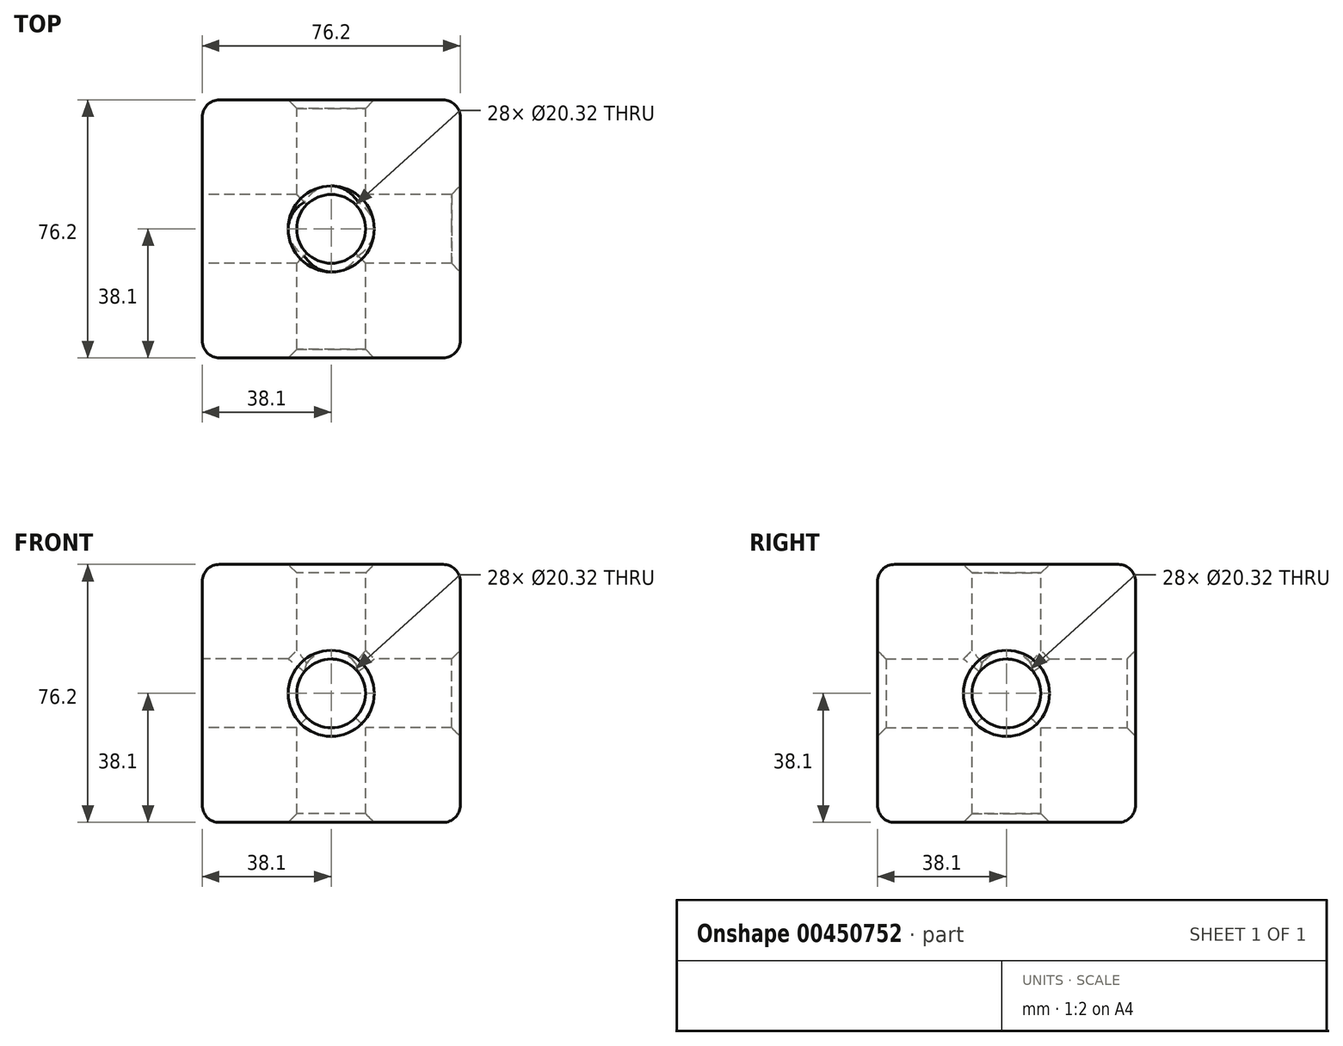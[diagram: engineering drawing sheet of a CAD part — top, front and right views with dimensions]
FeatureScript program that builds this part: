
annotation { "Feature Type Name" : "Feature", "Feature Type Description" : "" }
export const myFeature = defineFeature(function(context is Context, id is Id, definition is map)
    precondition{}
    {
        {
            var Q0;
            Q0=qCreatedBy(makeId("Top.planeOp"),FACE);
            var sketch = newSketch(context, id + "F0", { "sketchPlane" : qUnion([Q0])});
            skLineSegment(sketch, "E0.bottom", {"start": v(-38.1, 38.1) * mm, "end": v(38.1, 38.1) * mm});
            skLineSegment(sketch, "E0.top", {"start": v(-38.1, -38.1) * mm, "end": v(38.1, -38.1) * mm});
            skLineSegment(sketch, "E0.left", {"start": v(-38.1, 38.1) * mm, "end": v(-38.1, -38.1) * mm});
            skLineSegment(sketch, "E0.right", {"start": v(38.1, 38.1) * mm, "end": v(38.1, -38.1) * mm});
            skPoint(sketch, "E0.middle", {"position": v(0, 0) * mm});
            skSolve(sketch);
        }
        {
            var Q0;
            Q0 = qSketchRegion(id + "F0", true);
            extrude(context, id + "F1", {"entities" : qUnion([Q0]), "endBound" : BoundingType.SYMMETRIC, "depth" : 76.2 * mm});
        }
        {
            var Q0;
            Q0=qCreatedBy(makeId("Top.planeOp"),FACE);
            var sketch = newSketch(context, id + "F2", { "sketchPlane" : qUnion([Q0])});
            skCircle(sketch, "E1", {"center": v(0, 0) * mm, "radius": 10.16 * mm});
            skSolve(sketch);
        }
        {
            var Q0;
            Q0 = qSketchRegion(id + "F2", true);
            extrude(context, id + "F3", {"entities" : qUnion([Q0]), "operationType" : NewBodyOperationType.REMOVE, "endBound" : BoundingType.SYMMETRIC, "oppositeDirection" : true, "depth" : 319.53 * mm});
        }
        {
            var Q0;
            Q0=makeQuery(id+"F1.opExtrude","SWEPT_FACE",FACE,{"disambiguationData":[OSD([sQuery(id+"F0.wireOp",EDGE,"E0.left")])]});
            var sketch = newSketch(context, id + "F4", { "sketchPlane" : qUnion([Q0])});
            skCircle(sketch, "E2", {"center": v(0, 0) * mm, "radius": 10.16 * mm});
            skSolve(sketch);
        }
        {
            var Q0;
            Q0 = qSketchRegion(id + "F4", true);
            extrude(context, id + "F5", {"entities" : qUnion([Q0]), "operationType" : NewBodyOperationType.REMOVE, "oppositeDirection" : true, "depth" : 130.05 * mm});
        }
        {
            var Q0;
            Q0=makeQuery(id+"F1.opExtrude","SWEPT_FACE",FACE,{"disambiguationData":[OSD([sQuery(id+"F0.wireOp",EDGE,"E0.bottom")])]});
            var sketch = newSketch(context, id + "F6", { "sketchPlane" : qUnion([Q0])});
            skCircle(sketch, "E3", {"center": v(0, 0) * mm, "radius": 10.16 * mm});
            skSolve(sketch);
        }
        {
            var Q0;
            Q0 = qSketchRegion(id + "F6", true);
            extrude(context, id + "F7", {"entities" : qUnion([Q0]), "operationType" : NewBodyOperationType.REMOVE, "oppositeDirection" : true, "depth" : 100.08 * mm});
        }
        {
            var Q0;
            Q0=makeQuery(id+"F1.opExtrude","SWEPT_EDGE",EDGE,{"disambiguationData":[OSD([sQuery(id+"F0.wireOp",EDGE,"E0.bottom"),sQuery(id+"F0.wireOp",EDGE,"E0.left")])]});
            var Q1;
            Q1=makeQuery(id+"F1.opExtrude","CAP_EDGE",EDGE,{"disambiguationData":[OSD([sQuery(id+"F0.wireOp",EDGE,"E0.left")])],"isStart":true});
            var Q2;
            Q2=makeQuery(id+"F1.opExtrude","SWEPT_EDGE",EDGE,{"disambiguationData":[OSD([sQuery(id+"F0.wireOp",EDGE,"E0.top"),sQuery(id+"F0.wireOp",EDGE,"E0.left")])]});
            var Q3;
            Q3=makeQuery(id+"F1.opExtrude","CAP_EDGE",EDGE,{"disambiguationData":[OSD([sQuery(id+"F0.wireOp",EDGE,"E0.left")])],"isStart":false});
            var Q4;
            Q4=makeQuery(id+"F1.opExtrude","CAP_EDGE",EDGE,{"disambiguationData":[OSD([sQuery(id+"F0.wireOp",EDGE,"E0.bottom")])],"isStart":false});
            var Q5;
            Q5=makeQuery(id+"F1.opExtrude","CAP_EDGE",EDGE,{"disambiguationData":[OSD([sQuery(id+"F0.wireOp",EDGE,"E0.right")])],"isStart":false});
            var Q6;
            Q6=makeQuery(id+"F1.opExtrude","CAP_EDGE",EDGE,{"disambiguationData":[OSD([sQuery(id+"F0.wireOp",EDGE,"E0.top")])],"isStart":false});
            var Q7;
            Q7=makeQuery(id+"F1.opExtrude","SWEPT_EDGE",EDGE,{"disambiguationData":[OSD([sQuery(id+"F0.wireOp",EDGE,"E0.bottom"),sQuery(id+"F0.wireOp",EDGE,"E0.right")])]});
            var Q8;
            Q8=makeQuery(id+"F1.opExtrude","SWEPT_EDGE",EDGE,{"disambiguationData":[OSD([sQuery(id+"F0.wireOp",EDGE,"E0.top"),sQuery(id+"F0.wireOp",EDGE,"E0.right")])]});
            var Q9;
            Q9=makeQuery(id+"F1.opExtrude","CAP_EDGE",EDGE,{"disambiguationData":[OSD([sQuery(id+"F0.wireOp",EDGE,"E0.right")])],"isStart":true});
            var Q10;
            Q10=makeQuery(id+"F1.opExtrude","CAP_EDGE",EDGE,{"disambiguationData":[OSD([sQuery(id+"F0.wireOp",EDGE,"E0.bottom")])],"isStart":true});
            var Q11;
            Q11=makeQuery(id+"F1.opExtrude","CAP_EDGE",EDGE,{"disambiguationData":[OSD([sQuery(id+"F0.wireOp",EDGE,"E0.top")])],"isStart":true});
            fillet(context, id + "F8", {"entities" : qUnion([Q0, Q1, Q2, Q3, Q4, Q5, Q6, Q7, Q8, Q9, Q10, Q11]), "radius" : 5.08 * mm, "tangentPropagation" : true, "allowEdgeOverflow" : false});
        }
        {
            var Q0;
            Q0=makeQuery(id+"F3.boolean.opBoolean","INTERSECT",EDGE,{"derivedFrom":[makeQuery(id+"F1.opExtrude","CAP_FACE",FACE,{"disambiguationData":[OSD([sQuery(id+"F0.wireOp",EDGE,"E0.bottom"),sQuery(id+"F0.wireOp",EDGE,"E0.top"),sQuery(id+"F0.wireOp",EDGE,"E0.left"),sQuery(id+"F0.wireOp",EDGE,"E0.right")])],"isStart":true}),makeQuery(id+"F3.opExtrude","SWEPT_FACE",FACE,{"disambiguationData":[OSD([sQuery(id+"F2.wireOp",EDGE,"E1")])]})]});
            var Q1;
            Q1=makeQuery(id+"F1.opExtrude","SWEPT_FACE",FACE,{"disambiguationData":[OSD([sQuery(id+"F0.wireOp",EDGE,"E0.bottom")])]});
            var Q2;
            Q2=makeQuery(id+"F5.boolean.opBoolean","COPY",EDGE,{"derivedFrom":makeQuery(id+"F5.opExtrude","CAP_EDGE",EDGE,{"disambiguationData":[OSD([sQuery(id+"F4.wireOp",EDGE,"E2")])],"isStart":true})});
            var Q3;
            {var subQ0=makeQuery(id+"F3.boolean.opBoolean","COPY",FACE,{"derivedFrom":makeQuery(id+"F3.opExtrude","SWEPT_FACE",FACE,{"disambiguationData":[OSD([sQuery(id+"F2.wireOp",EDGE,"E1")])]})});Q3=makeQuery(id+"F5.boolean.opBoolean","SPLIT",FACE,{"disambiguationData":[TD([makeQuery(id+"F1.opExtrude","CAP_FACE",FACE,{"disambiguationData":[OSD([sQuery(id+"F0.wireOp",EDGE,"E0.bottom"),sQuery(id+"F0.wireOp",EDGE,"E0.top"),sQuery(id+"F0.wireOp",EDGE,"E0.left"),sQuery(id+"F0.wireOp",EDGE,"E0.right")])],"isStart":false})])],"derivedFrom":subQ0});}
            var Q4;
            Q4=makeQuery(id+"F7.boolean.opBoolean","INTERSECT",EDGE,{"derivedFrom":[makeQuery(id+"F1.opExtrude","SWEPT_FACE",FACE,{"disambiguationData":[OSD([sQuery(id+"F0.wireOp",EDGE,"E0.top")])]}),makeQuery(id+"F7.opExtrude","SWEPT_FACE",FACE,{"disambiguationData":[OSD([sQuery(id+"F6.wireOp",EDGE,"E3")])]})]});
            var Q5;
            Q5=makeQuery(id+"F1.opExtrude","SWEPT_FACE",FACE,{"disambiguationData":[OSD([sQuery(id+"F0.wireOp",EDGE,"E0.right")])]});
            chamfer(context, id + "F9", {"entities" : qUnion([Q0, Q1, Q2, Q3, Q4, Q5]), "width" : 2.54 * mm, "tangentPropagation" : true});
        }
    });
